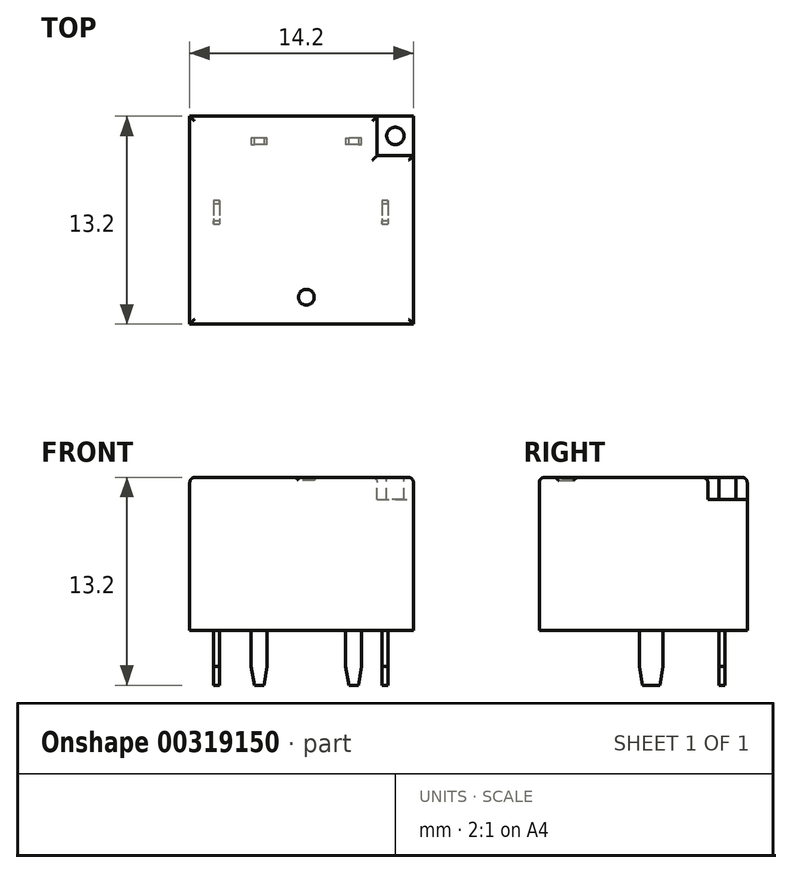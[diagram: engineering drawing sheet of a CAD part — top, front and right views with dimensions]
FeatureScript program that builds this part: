
annotation { "Feature Type Name" : "Feature", "Feature Type Description" : "" }
export const myFeature = defineFeature(function(context is Context, id is Id, definition is map)
    precondition{}
    {
        {
            var Q0;
            Q0=qCreatedBy(makeId("Top.planeOp"),FACE);
            var sketch = newSketch(context, id + "F0", { "sketchPlane" : qUnion([Q0])});
            skLineSegment(sketch, "E0.bottom", {"start": v(-5.5, 0.75) * mm, "end": v(-5.9, 0.75) * mm});
            skLineSegment(sketch, "E0.top", {"start": v(-5.5, -0.75) * mm, "end": v(-5.9, -0.75) * mm});
            skLineSegment(sketch, "E0.left", {"start": v(-5.5, 0.75) * mm, "end": v(-5.5, -0.75) * mm});
            skLineSegment(sketch, "E0.right", {"start": v(-5.9, 0.75) * mm, "end": v(-5.9, -0.75) * mm});
            skPoint(sketch, "E0.middle", {"position": v(-5.7, 0) * mm});
            skLineSegment(sketch, "E1.bottom", {"start": v(5.2, 0.75) * mm, "end": v(4.8, 0.75) * mm});
            skLineSegment(sketch, "E1.top", {"start": v(5.2, -0.75) * mm, "end": v(4.8, -0.75) * mm});
            skLineSegment(sketch, "E1.left", {"start": v(5.2, 0.75) * mm, "end": v(5.2, -0.75) * mm});
            skLineSegment(sketch, "E1.right", {"start": v(4.8, 0.75) * mm, "end": v(4.8, -0.75) * mm});
            skPoint(sketch, "E1.middle", {"position": v(5, 0) * mm});
            skLineSegment(sketch, "E2.bottom", {"start": v(0.75, -5.2) * mm, "end": v(-0.75, -5.2) * mm});
            skLineSegment(sketch, "E2.top", {"start": v(0.75, -5.6) * mm, "end": v(-0.75, -5.6) * mm});
            skLineSegment(sketch, "E2.left", {"start": v(0.75, -5.2) * mm, "end": v(0.75, -5.6) * mm});
            skLineSegment(sketch, "E2.right", {"start": v(-0.75, -5.2) * mm, "end": v(-0.75, -5.6) * mm});
            skPoint(sketch, "E2.middle", {"position": v(0, -5.4) * mm});
            skLineSegment(sketch, "E3.bottom", {"start": v(-2.5, 4.7) * mm, "end": v(-3.5, 4.7) * mm});
            skLineSegment(sketch, "E3.top", {"start": v(-2.5, 4.3) * mm, "end": v(-3.5, 4.3) * mm});
            skLineSegment(sketch, "E3.left", {"start": v(-2.5, 4.7) * mm, "end": v(-2.5, 4.3) * mm});
            skLineSegment(sketch, "E3.right", {"start": v(-3.5, 4.7) * mm, "end": v(-3.5, 4.3) * mm});
            skPoint(sketch, "E3.middle", {"position": v(-3, 4.5) * mm});
            skLineSegment(sketch, "E4.bottom", {"start": v(3.5, 4.3) * mm, "end": v(2.5, 4.3) * mm});
            skLineSegment(sketch, "E4.top", {"start": v(3.5, 4.7) * mm, "end": v(2.5, 4.7) * mm});
            skLineSegment(sketch, "E4.left", {"start": v(3.5, 4.3) * mm, "end": v(3.5, 4.7) * mm});
            skLineSegment(sketch, "E4.right", {"start": v(2.5, 4.3) * mm, "end": v(2.5, 4.7) * mm});
            skPoint(sketch, "E4.middle", {"position": v(3, 4.5) * mm});
            skSolve(sketch);
        }
        {
            var Q0;
            Q0=qCreatedBy(makeId("Top.planeOp"),FACE);
            var sketch = newSketch(context, id + "F1", { "sketchPlane" : qUnion([Q0])});
            skLineSegment(sketch, "E5.bottom", {"start": v(-7.4, -7.1) * mm, "end": v(6.8, -7.1) * mm});
            skLineSegment(sketch, "E5.top", {"start": v(-7.4, 6.1) * mm, "end": v(6.8, 6.1) * mm});
            skLineSegment(sketch, "E5.left", {"start": v(-7.4, -7.1) * mm, "end": v(-7.4, 6.1) * mm});
            skLineSegment(sketch, "E5.right", {"start": v(6.8, -7.1) * mm, "end": v(6.8, 6.1) * mm});
            skSolve(sketch);
        }
        {
            var Q0;
            Q0=makeQuery(id+"F1.imprint","IMPRINT",FACE,{"disambiguationData":[TD([[makeQuery(id+"F1.imprint","IMPRINT",EDGE,{"derivedFrom":sQuery(id+"F1.wireOp",EDGE,"E5.bottom")}),1.0]])]});
            extrude(context, id + "F2", {"entities" : qUnion([Q0]), "depth" : 9.7 * mm});
        }
        {
            var Q0;
            Q0=qSketchRegion(id+"F0",true);
            extrude(context, id + "F3", {"entities" : qUnion([Q0]), "oppositeDirection" : true, "depth" : 3.5 * mm});
        }
        {
            var Q0;
            Q0=makeQuery(id+"F2.opExtrude","CAP_FACE",FACE,{"disambiguationData":[OSD([sQuery(id+"F1.wireOp",EDGE,"E5.bottom"),sQuery(id+"F1.wireOp",EDGE,"E5.top"),sQuery(id+"F1.wireOp",EDGE,"E5.left"),sQuery(id+"F1.wireOp",EDGE,"E5.right")])],"isStart":false});
            var sketch = newSketch(context, id + "F4", { "sketchPlane" : qUnion([Q0])});
            skCircle(sketch, "E6", {"center": v(5.65, 4.85) * mm, "radius": 0.55 * mm});
            skLineSegment(sketch, "E7.bottom", {"start": v(4.5, 6.1) * mm, "end": v(6.8, 6.1) * mm});
            skLineSegment(sketch, "E7.top", {"start": v(4.5, 3.6) * mm, "end": v(6.8, 3.6) * mm});
            skLineSegment(sketch, "E7.left", {"start": v(4.5, 6.1) * mm, "end": v(4.5, 3.6) * mm});
            skLineSegment(sketch, "E7.right", {"start": v(6.8, 6.1) * mm, "end": v(6.8, 3.6) * mm});
            skCircle(sketch, "E8", {"center": v(0, -5.4) * mm, "radius": 0.5 * mm});
            skPoint(sketch, "E9", {"position": v(5.65, 3.6) * mm});
            skPoint(sketch, "E10", {"position": v(4.5, 4.85) * mm});
            skSolve(sketch);
        }
        {
            var Q0;
            Q0=makeQuery(id+"F4.imprint","IMPRINT",FACE,{"disambiguationData":[TD([[makeQuery(id+"F4.imprint","IMPRINT",EDGE,{"derivedFrom":sQuery(id+"F4.wireOp",EDGE,"E6")}),-1.0]])]});
            extrude(context, id + "F5", {"entities" : qUnion([Q0]), "operationType" : NewBodyOperationType.REMOVE, "oppositeDirection" : true, "depth" : 1.4 * mm});
        }
        {
            var Q0;
            Q0=makeQuery(id+"F4.imprint","IMPRINT",FACE,{"disambiguationData":[TD([[makeQuery(id+"F4.imprint","IMPRINT",EDGE,{"derivedFrom":sQuery(id+"F4.wireOp",EDGE,"E8")}),1.0]])]});
            extrude(context, id + "F6", {"entities" : qUnion([Q0]), "operationType" : NewBodyOperationType.REMOVE, "oppositeDirection" : true, "depth" : 0.2 * mm});
        }
        {
            var Q0;
            {var subQ0=sQuery(id+"F1.wireOp",EDGE,"E5.left");var subQ1=sQuery(id+"F1.wireOp",EDGE,"E5.top");var subQ2=sQuery(id+"F1.wireOp",EDGE,"E5.right");var subQ3=sQuery(id+"F1.wireOp",EDGE,"E5.bottom");Q0=makeQuery(id+"F5.boolean.opBoolean","SPLIT",FACE,{"disambiguationData":[TD([makeQuery(id+"F2.opExtrude","SWEPT_FACE",FACE,{"disambiguationData":[OSD([subQ3])]})])],"derivedFrom":makeQuery(id+"F2.opExtrude","CAP_FACE",FACE,{"disambiguationData":[OSD([subQ3,subQ1,subQ0,subQ2])],"isStart":false})});}
            fillet(context, id + "F7", {"entities" : qUnion([Q0]), "radius" : 0.3 * mm, "tangentPropagation" : true, "allowEdgeOverflow" : false});
        }
        {
            var Q0;
            Q0=makeQuery(id+"F3.opExtrude","CAP_EDGE",EDGE,{"disambiguationData":[OSD([sQuery(id+"F0.wireOp",EDGE,"E0.top")])],"isStart":false});
            var Q1;
            Q1=makeQuery(id+"F3.opExtrude","CAP_EDGE",EDGE,{"disambiguationData":[OSD([sQuery(id+"F0.wireOp",EDGE,"E0.bottom")])],"isStart":false});
            var Q2;
            Q2=makeQuery(id+"F3.opExtrude","CAP_EDGE",EDGE,{"disambiguationData":[OSD([sQuery(id+"F0.wireOp",EDGE,"E2.left")])],"isStart":false});
            var Q3;
            Q3=makeQuery(id+"F3.opExtrude","CAP_EDGE",EDGE,{"disambiguationData":[OSD([sQuery(id+"F0.wireOp",EDGE,"E2.right")])],"isStart":false});
            var Q4;
            Q4=makeQuery(id+"F3.opExtrude","CAP_EDGE",EDGE,{"disambiguationData":[OSD([sQuery(id+"F0.wireOp",EDGE,"E3.left")])],"isStart":false});
            var Q5;
            Q5=makeQuery(id+"F3.opExtrude","CAP_EDGE",EDGE,{"disambiguationData":[OSD([sQuery(id+"F0.wireOp",EDGE,"E3.right")])],"isStart":false});
            var Q6;
            Q6=makeQuery(id+"F3.opExtrude","CAP_EDGE",EDGE,{"disambiguationData":[OSD([sQuery(id+"F0.wireOp",EDGE,"E4.right")])],"isStart":false});
            var Q7;
            Q7=makeQuery(id+"F3.opExtrude","CAP_EDGE",EDGE,{"disambiguationData":[OSD([sQuery(id+"F0.wireOp",EDGE,"E4.left")])],"isStart":false});
            var Q8;
            Q8=makeQuery(id+"F3.opExtrude","CAP_EDGE",EDGE,{"disambiguationData":[OSD([sQuery(id+"F0.wireOp",EDGE,"E1.top")])],"isStart":false});
            var Q9;
            Q9=makeQuery(id+"F3.opExtrude","CAP_EDGE",EDGE,{"disambiguationData":[OSD([sQuery(id+"F0.wireOp",EDGE,"E1.bottom")])],"isStart":false});
            chamfer(context, id + "F8", {"entities" : qUnion([Q0, Q1, Q2, Q3, Q4, Q5, Q6, Q7, Q8, Q9]), "chamferType" : ChamferType.TWO_OFFSETS, "width1" : 0.2 * mm, "oppositeDirection" : false, "width2" : 1.2 * mm, "tangentPropagation" : true});
        }
        {
            var Q0;
            Q0=makeQuery(id+"F3.opExtrude","SWEPT_BODY",BODY,{"disambiguationData":[OSD([sQuery(id+"F0.wireOp",EDGE,"E2.bottom"),sQuery(id+"F0.wireOp",EDGE,"E2.top"),sQuery(id+"F0.wireOp",EDGE,"E2.left"),sQuery(id+"F0.wireOp",EDGE,"E2.right")])]});
            deleteBodies(context, id + "F9", {"entities" : qUnion([Q0])});
        }
    });
